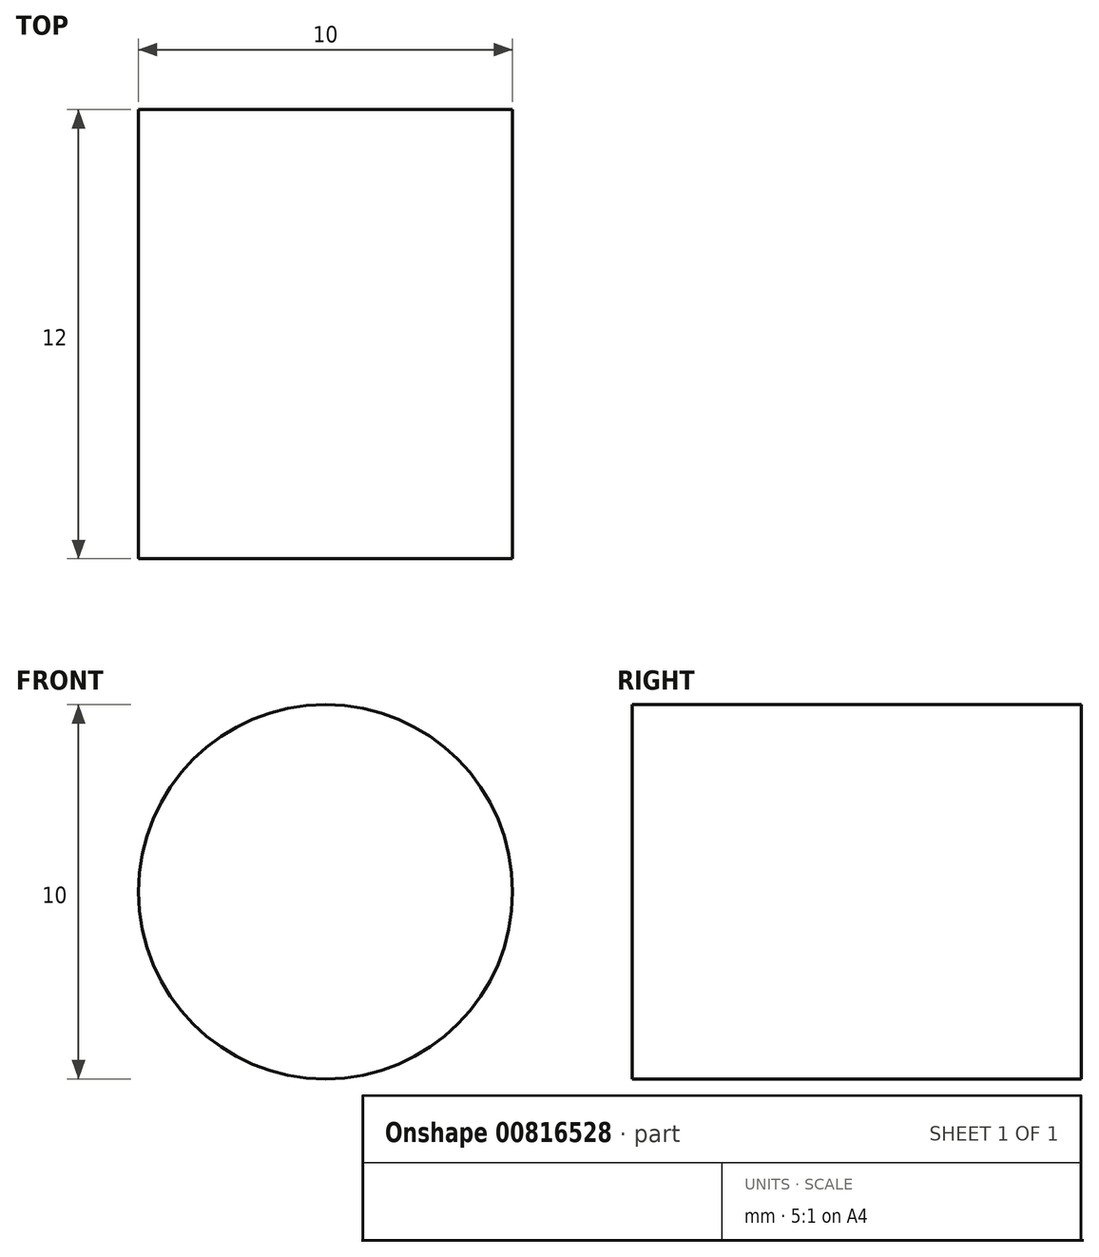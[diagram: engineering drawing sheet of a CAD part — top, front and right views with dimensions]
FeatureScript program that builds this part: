
annotation { "Feature Type Name" : "Feature", "Feature Type Description" : "" }
export const myFeature = defineFeature(function(context is Context, id is Id, definition is map)
    precondition{}
    {
        {
            var Q0;
            Q0=qCreatedBy(makeId("Front.planeOp"),FACE);
            var sketch = newSketch(context, id + "F0", { "sketchPlane" : qUnion([Q0])});
            skCircle(sketch, "E0", {"center": v(0, 0) * mm, "radius": 5 * mm});
            skSolve(sketch);
        }
        {
            var Q0;
            Q0 = qSketchRegion(id + "F0", true);
            extrude(context, id + "F1", {"entities" : qUnion([Q0]), "depth" : 12 * mm, "offsetDistance" : 25 * mm});
        }
    });
